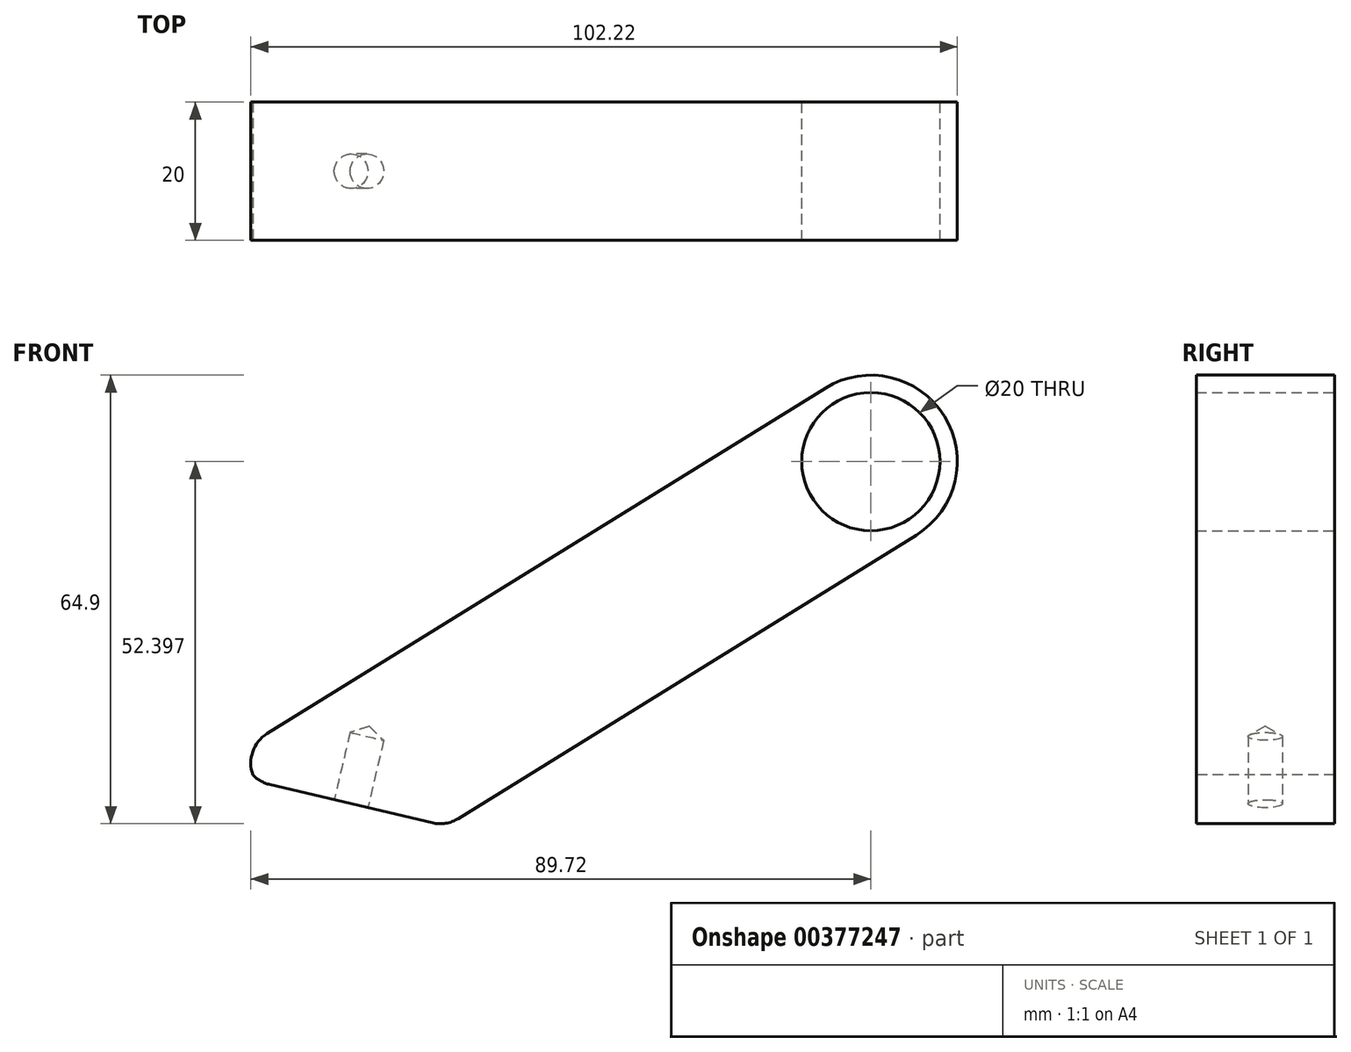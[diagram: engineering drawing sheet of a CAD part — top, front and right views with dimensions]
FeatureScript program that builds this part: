
annotation { "Feature Type Name" : "Feature", "Feature Type Description" : "" }
export const myFeature = defineFeature(function(context is Context, id is Id, definition is map)
    precondition{}
    {
        {
            var Q0;
            Q0=qCreatedBy(makeId("Front.planeOp"),FACE);
            var sketch = newSketch(context, id + "F0", { "sketchPlane" : qUnion([Q0])});
            skCircle(sketch, "E0", {"center": v(4.72, 17.37) * mm, "radius": 12.5 * mm});
            skCircle(sketch, "E1", {"center": v(4.72, 17.37) * mm, "radius": 10 * mm});
            skLineSegment(sketch, "E2", {"start": v(-86.89, -24.64) * mm, "end": v(-1.86, 28) * mm});
            skLineSegment(sketch, "E3", {"start": v(-73.73, -45.9) * mm, "end": v(11.3, 6.74) * mm});
            skLineSegment(sketch, "E4", {"start": v(-86.89, -24.64) * mm, "end": v(-73.73, -45.9) * mm});
            skSolve(sketch);
        }
        {
            var Q0;
            Q0=makeQuery(id+"F0.imprint","IMPRINT",FACE,{"disambiguationData":[TD([[makeQuery(id+"F0.imprint","IMPRINT",EDGE,{"derivedFrom":sQuery(id+"F0.wireOp",EDGE,"E1")}),-1.0]])]});
            var Q1;
            {var subQ0=sQuery(id+"F0.wireOp",EDGE,"E2");Q1=makeQuery(id+"F0.imprint","IMPRINT",FACE,{"disambiguationData":[TD([[makeQuery(id+"F0.imprint","IMPRINT",EDGE,{"derivedFrom":subQ0}),-1.0]])]});}
            var Q2;
            Q2=makeQuery(id+"F0.imprint","IMPRINT",FACE,{"disambiguationData":[TD([[makeQuery(id+"F0.imprint","IMPRINT",EDGE,{"derivedFrom":sQuery(id+"F0.wireOp",EDGE,"9e393df0-6f5c-4755-bc6f-85b92e551ec1")}),-1.0]])]});
            var Q3;
            Q3=makeQuery(id+"F0.imprint","IMPRINT",FACE,{"disambiguationData":[TD([[makeQuery(id+"F0.imprint","IMPRINT",EDGE,{"derivedFrom":sQuery(id+"F0.wireOp",EDGE,"9e393df0-6f5c-4755-bc6f-85b92e551ec1")}),1.0]])]});
            extrude(context, id + "F1", {"entities" : qUnion([Q0, Q1, Q2, Q3]), "depth" : 20 * mm});
        }
        {
            var Q0;
            Q0=makeQuery(id+"F1.opExtrude","SWEPT_EDGE",EDGE,{"disambiguationData":[OSD([sQuery(id+"F0.wireOp",EDGE,"E3"),sQuery(id+"F0.wireOp",EDGE,"E4")])]});
            chamfer(context, id + "F2", {"entities" : qUnion([Q0]), "width" : 20 * mm});
        }
        {
            var Q0;
            Q0=makeQuery(id+"F2.opChamfer","BLEND_FACE",FACE,{"disambiguationData":[OSD([sQuery(id+"F0.wireOp",EDGE,"E3"),sQuery(id+"F0.wireOp",EDGE,"E4")])]});
            var sketch = newSketch(context, id + "F3", { "sketchPlane" : qUnion([Q0])});
            skLineSegment(sketch, "E5.0", {"start": v(-75.4, 20) * mm, "end": v(-47.11, 20) * mm});
            skLineSegment(sketch, "E5.1", {"start": v(-75.4, 0) * mm, "end": v(-75.4, 20) * mm});
            skLineSegment(sketch, "E5.2", {"start": v(-47.11, 0) * mm, "end": v(-75.4, 0) * mm});
            skLineSegment(sketch, "E5.3", {"start": v(-47.11, 20) * mm, "end": v(-47.11, 0) * mm});
            skPoint(sketch, "E6", {"position": v(-61.26, 10) * mm});
            skSolve(sketch);
        }
        {
            var Q0;
            Q0=sQuery(id+"F3.wireOp",VERTEX,"E6");
            var Q1;
            Q1=makeQuery(id+"F1.opExtrude","SWEPT_BODY",BODY,{"disambiguationData":[OSD([sQuery(id+"F0.wireOp",EDGE,"E0"),sQuery(id+"F0.wireOp",EDGE,"E1"),sQuery(id+"F0.wireOp",EDGE,"E2"),sQuery(id+"F0.wireOp",EDGE,"E3"),sQuery(id+"F0.wireOp",EDGE,"E4")])]});
            hole(context, id + "F4", {"style" : HoleStyle.SIMPLE, "endStyle" : HoleEndStyle.BLIND, "holeDiameter" : 5 * mm, "holeDepth" : 10 * mm, "isTappedThrough" : true, "tappedDepth" : 12 * mm, "tapClearance" : 3, "startFromSketch" : true, "locations" : qUnion([Q0]), "scope" : qUnion([Q1])});
        }
        {
            var Q0;
            Q0=makeQuery(id+"F1.opExtrude","SWEPT_EDGE",EDGE,{"disambiguationData":[OSD([sQuery(id+"F0.wireOp",EDGE,"E2"),sQuery(id+"F0.wireOp",EDGE,"E4")])]});
            var Q1;
            {var subQ0=sQuery(id+"F0.wireOp",EDGE,"E4");Q1=makeQuery(id+"F2.opChamfer","BLEND_EDGE",EDGE,{"blendedFrom":[makeQuery(id+"F1.opExtrude","SWEPT_EDGE",EDGE,{"disambiguationData":[OSD([sQuery(id+"F0.wireOp",EDGE,"E3"),subQ0])]}),makeQuery(id+"F1.opExtrude","SWEPT_FACE",FACE,{"disambiguationData":[OSD([subQ0])]})],"blendedInto":[makeQuery(id+"F1.opExtrude","SWEPT_FACE",FACE,{"disambiguationData":[OSD([subQ0])]})]});}
            var Q2;
            {var subQ0=sQuery(id+"F0.wireOp",EDGE,"E3");Q2=makeQuery(id+"F2.opChamfer","BLEND_EDGE",EDGE,{"blendedFrom":[makeQuery(id+"F1.opExtrude","SWEPT_EDGE",EDGE,{"disambiguationData":[OSD([subQ0,sQuery(id+"F0.wireOp",EDGE,"E4")])]}),makeQuery(id+"F1.opExtrude","SWEPT_FACE",FACE,{"disambiguationData":[OSD([subQ0])]})],"blendedInto":[makeQuery(id+"F1.opExtrude","SWEPT_FACE",FACE,{"disambiguationData":[OSD([subQ0])]})]});}
            fillet(context, id + "F5", {"entities" : qUnion([Q0, Q1, Q2]), "radius" : 5 * mm, "tangentPropagation" : true, "allowEdgeOverflow" : false});
        }
    });
